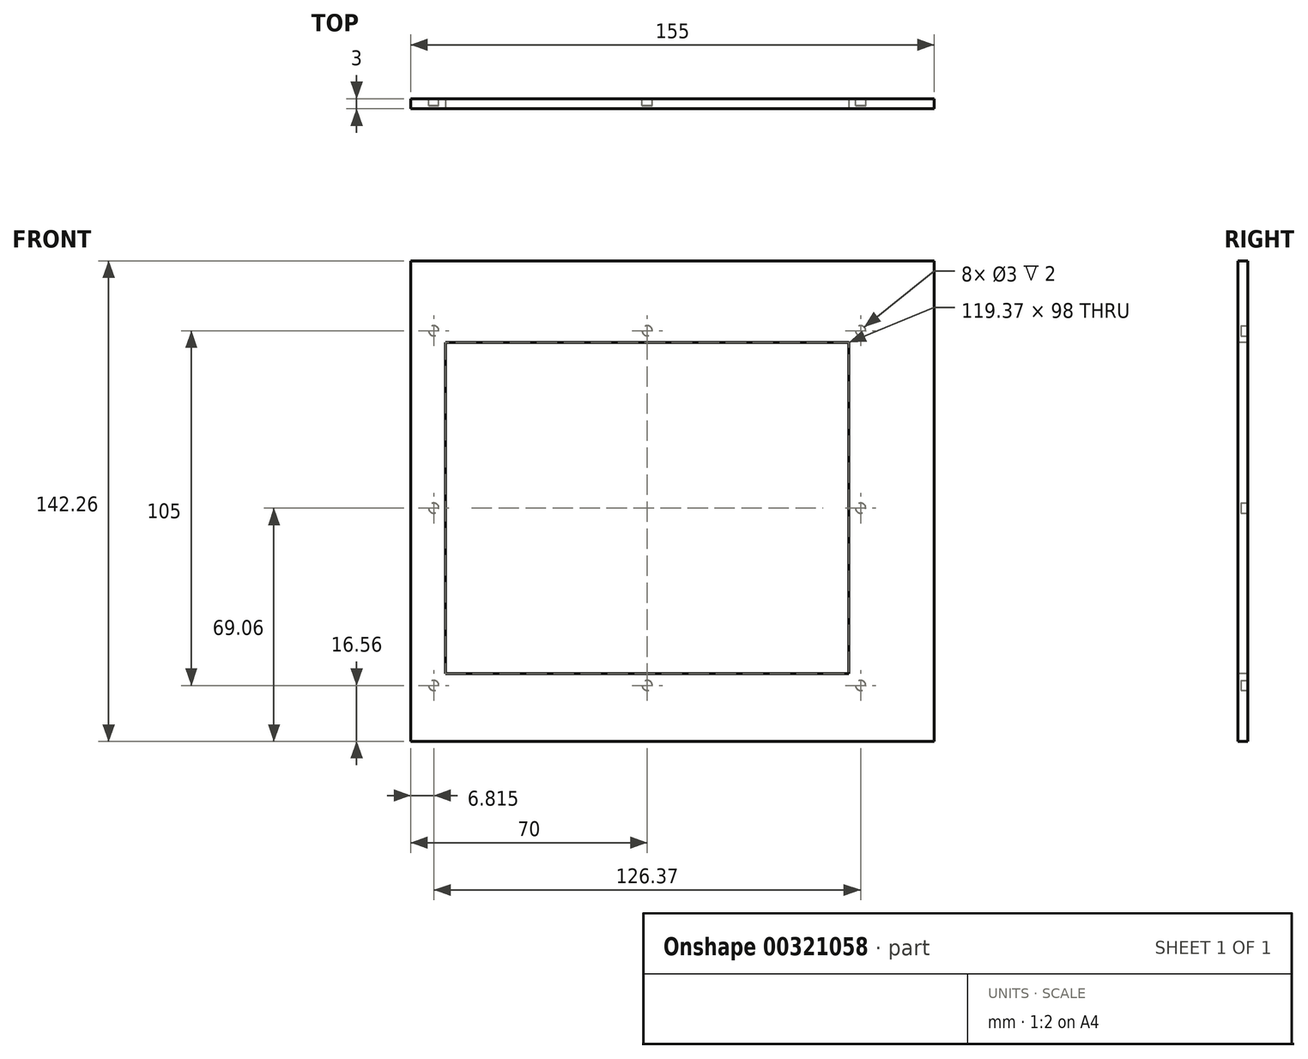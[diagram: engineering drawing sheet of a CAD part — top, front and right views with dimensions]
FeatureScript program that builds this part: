
annotation { "Feature Type Name" : "Feature", "Feature Type Description" : "" }
export const myFeature = defineFeature(function(context is Context, id is Id, definition is map)
    precondition{}
    {
        {
            var Q0;
            Q0=qCreatedBy(makeId("Front.planeOp"),FACE);
            var sketch = newSketch(context, id + "F0", { "sketchPlane" : qUnion([Q0])});
            skLineSegment(sketch, "E0.bottom", {"start": v(77.5, 65.38) * mm, "end": v(-77.5, 65.38) * mm});
            skLineSegment(sketch, "E0.top", {"start": v(77.5, -65.38) * mm, "end": v(-77.5, -65.38) * mm});
            skLineSegment(sketch, "E0.left", {"start": v(77.5, 65.38) * mm, "end": v(77.5, -65.38) * mm});
            skLineSegment(sketch, "E0.right", {"start": v(-77.5, 65.38) * mm, "end": v(-77.5, -65.38) * mm});
            skPoint(sketch, "E0.middle", {"position": v(0, 0) * mm});
            skSolve(sketch);
        }
        {
            var Q0;
            Q0=qSketchRegion(id+"F0",true);
            extrude(context, id + "F1", {"entities" : qUnion([Q0]), "depth" : 3 * mm});
        }
        {
            var Q0;
            Q0=makeQuery(id+"F1.opExtrude","CAP_FACE",FACE,{"disambiguationData":[OSD([sQuery(id+"F0.wireOp",EDGE,"E0.bottom"),sQuery(id+"F0.wireOp",EDGE,"E0.top"),sQuery(id+"F0.wireOp",EDGE,"E0.left"),sQuery(id+"F0.wireOp",EDGE,"E0.right")])],"isStart":true});
            var sketch = newSketch(context, id + "F2", { "sketchPlane" : qUnion([Q0])});
            skLineSegment(sketch, "E1.bottom", {"start": v(64.19, 49.68) * mm, "end": v(-49.19, 49.68) * mm});
            skLineSegment(sketch, "E1.top", {"start": v(64.19, -42.32) * mm, "end": v(-49.19, -42.32) * mm});
            skLineSegment(sketch, "E1.left", {"start": v(64.19, 49.68) * mm, "end": v(64.18, -42.32) * mm});
            skLineSegment(sketch, "E1.right", {"start": v(-49.19, 49.68) * mm, "end": v(-49.19, -42.32) * mm});
            skLineSegment(sketch, "E2", {"start": v(64.19, 49.68) * mm, "end": v(-49.19, -42.32) * mm, "construction": true});
            skLineSegment(sketch, "E3", {"start": v(-49.19, 49.68) * mm, "end": v(64.19, -42.32) * mm, "construction": true});
            skLineSegment(sketch, "E4.bottom", {"start": v(64.19, 49.68) * mm, "end": v(7.5, 49.68) * mm, "construction": true});
            skLineSegment(sketch, "E4.top", {"start": v(64.19, -42.32) * mm, "end": v(7.5, -42.32) * mm, "construction": true});
            skLineSegment(sketch, "E4.left", {"start": v(64.18, 49.68) * mm, "end": v(64.18, -42.32) * mm, "construction": true});
            skLineSegment(sketch, "E4.right", {"start": v(7.5, 49.68) * mm, "end": v(7.5, -42.32) * mm, "construction": true});
            skSolve(sketch);
        }
        {
            var Q0;
            Q0 = qSketchRegion(id + "F2", true);
            extrude(context, id + "F3", {"entities" : qUnion([Q0]), "operationType" : NewBodyOperationType.REMOVE, "oppositeDirection" : true, "depth" : 25 * mm});
        }
        {
            var Q0;
            Q0=makeQuery(id+"F1.opExtrude","CAP_FACE",FACE,{"disambiguationData":[OSD([sQuery(id+"F0.wireOp",EDGE,"E0.bottom"),sQuery(id+"F0.wireOp",EDGE,"E0.top"),sQuery(id+"F0.wireOp",EDGE,"E0.left"),sQuery(id+"F0.wireOp",EDGE,"E0.right")])],"isStart":false});
            var sketch = newSketch(context, id + "F4", { "sketchPlane" : qUnion([Q0])});
            skLineSegment(sketch, "E5.bottom", {"start": v(-67.19, 52.68) * mm, "end": v(52.19, 52.68) * mm});
            skLineSegment(sketch, "E5.top", {"start": v(-67.18, -45.32) * mm, "end": v(52.19, -45.32) * mm});
            skLineSegment(sketch, "E5.left", {"start": v(-67.19, 52.68) * mm, "end": v(-67.18, -45.32) * mm});
            skLineSegment(sketch, "E5.right", {"start": v(52.19, 52.68) * mm, "end": v(52.19, -45.32) * mm});
            skSolve(sketch);
        }
        {
            var Q0;
            Q0 = qSketchRegion(id + "F4", true);
            extrude(context, id + "F5", {"entities" : qUnion([Q0]), "operationType" : NewBodyOperationType.REMOVE, "oppositeDirection" : true, "depth" : 25 * mm});
        }
        {
            var Q0;
            Q0=makeQuery(id+"F1.opExtrude","CAP_FACE",FACE,{"disambiguationData":[OSD([sQuery(id+"F0.wireOp",EDGE,"E0.bottom"),sQuery(id+"F0.wireOp",EDGE,"E0.top"),sQuery(id+"F0.wireOp",EDGE,"E0.left"),sQuery(id+"F0.wireOp",EDGE,"E0.right")])],"isStart":true});
            var sketch = newSketch(context, id + "F6", { "sketchPlane" : qUnion([Q0])});
            skLineSegment(sketch, "E6.bottom", {"start": v(-55.69, 56.18) * mm, "end": v(70.69, 56.18) * mm, "construction": true});
            skLineSegment(sketch, "E6.top", {"start": v(-55.69, -48.82) * mm, "end": v(70.69, -48.82) * mm, "construction": true});
            skLineSegment(sketch, "E6.left", {"start": v(-55.69, 56.18) * mm, "end": v(-55.69, -48.82) * mm, "construction": true});
            skLineSegment(sketch, "E6.right", {"start": v(70.69, 56.18) * mm, "end": v(70.69, -48.82) * mm, "construction": true});
            skCircle(sketch, "E7", {"center": v(-55.69, 56.18) * mm, "radius": 1.5 * mm});
            skCircle(sketch, "E8", {"center": v(70.69, 56.18) * mm, "radius": 1.5 * mm});
            skCircle(sketch, "E9", {"center": v(70.69, -48.82) * mm, "radius": 1.5 * mm});
            skCircle(sketch, "E10", {"center": v(-55.69, -48.82) * mm, "radius": 1.5 * mm});
            skCircle(sketch, "E11", {"center": v(7.5, -48.82) * mm, "radius": 1.5 * mm});
            skCircle(sketch, "E12", {"center": v(-55.69, 3.68) * mm, "radius": 1.5 * mm});
            skCircle(sketch, "E13", {"center": v(70.69, 3.68) * mm, "radius": 1.5 * mm});
            skCircle(sketch, "E14", {"center": v(7.5, 56.18) * mm, "radius": 1.5 * mm});
            skSolve(sketch);
        }
        {
            var Q0;
            Q0 = qSketchRegion(id + "F6", true);
            extrude(context, id + "F7", {"entities" : qUnion([Q0]), "operationType" : NewBodyOperationType.REMOVE, "oppositeDirection" : true, "depth" : 2 * mm});
        }
        {
            var Q0;
            Q0=makeQuery(id+"F1.opExtrude","SWEPT_FACE",FACE,{"disambiguationData":[OSD([sQuery(id+"F0.wireOp",EDGE,"E0.bottom")])]});
            var sketch = newSketch(context, id + "F8", { "sketchPlane" : qUnion([Q0])});
            skLineSegment(sketch, "E15.bottom", {"start": v(-77.5, 0) * mm, "end": v(77.5, 0) * mm});
            skLineSegment(sketch, "E15.top", {"start": v(-77.5, -3) * mm, "end": v(77.5, -3) * mm});
            skLineSegment(sketch, "E15.left", {"start": v(-77.5, 0) * mm, "end": v(-77.5, -3) * mm});
            skLineSegment(sketch, "E15.right", {"start": v(77.5, 0) * mm, "end": v(77.5, -3) * mm});
            skSolve(sketch);
        }
        {
            var Q0;
            Q0 = qSketchRegion(id + "F8", true);
            extrude(context, id + "F9", {"entities" : qUnion([Q0]), "operationType" : NewBodyOperationType.ADD, "depth" : 11.5 * mm});
        }
    });
